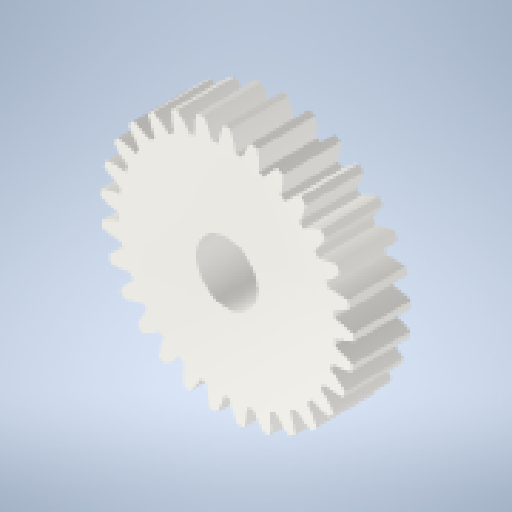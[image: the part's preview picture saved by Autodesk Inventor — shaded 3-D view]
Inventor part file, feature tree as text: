
AUTODESK INVENTOR PART (.ipt)
format: ipt  version: 2024 (Build 280153000, 153)  size: 290,304 bytes
history: native  units: mm (DEFAULTED — no unit token found)
features: plane x3, other x3, extrude x2, sketch x2
ambient origin geometry x8: Origin, YZ Plane, XZ Plane, XY Plane, X Axis, Y Axis, Z Axis, Center Point
bodies: Solid1 (feature_tree)
feature tree (10):
  extrude  "Extrusion1"  Depth=5.0mm TaperAngle=0.0deg
  plane  "Work Plane2"
  plane  "Work Plane8"
  plane  "Work Plane9"
  other  "Spur Gear"
  extrude  "Extrusion2"  Depth=10.0mm TaperAngle=0.0deg
  sketch  "Sketch1"  dims[d0=21.8mm d1=5.0mm d2=0.0mm]
  other  "Srf1"
  sketch  "Sketch3"  dims[d3=20.3mm d4=10.0mm d5=0.0mm d16=20.0mm d17=0.0mm d34=1.083308mm d39=0.0mm d41=0.0mm d43=20.0mm d46=20.0mm d47=0.0mm d48=0.0mm d49=5.3mm d50=10.0mm d51=0.0mm]
  other  "Pitch Diameter"
